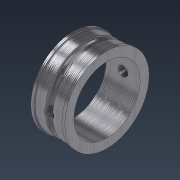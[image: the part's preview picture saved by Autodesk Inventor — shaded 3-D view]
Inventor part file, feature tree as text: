
AUTODESK INVENTOR PART (.ipt)
format: ipt  version: 2022 (Build 260153000, 153)  size: 174,080 bytes
history: native  units: mm
features: sketch x2, revolve x1, extrude x1
ambient origin geometry x8: Origin, YZ Plane, XZ Plane, XY Plane, X Axis, Y Axis, Z Axis, Center Point
bodies: Solid1 (feature_tree)
feature tree (4):
  revolve  "Revolution1"  [1 undecoded]
  extrude  "Extrusion1"  Depth=28.172mm
  sketch  "Sketch1"  dims[d0=100.0mm d1=3.0mm]
  sketch  "Sketch2"  dims[d3=55.0mm d4=28.172mm d5=90.0deg d6=8.0mm d7=0.0mm d8=0.0mm d9=2.5mm d10=1.0mm d11=70.0mm]
note: 1 required parameter value undecoded (feature->parameter linkage not recoverable at this tier; creation-order binding heuristic only, values carry confidence <= 0.55)
